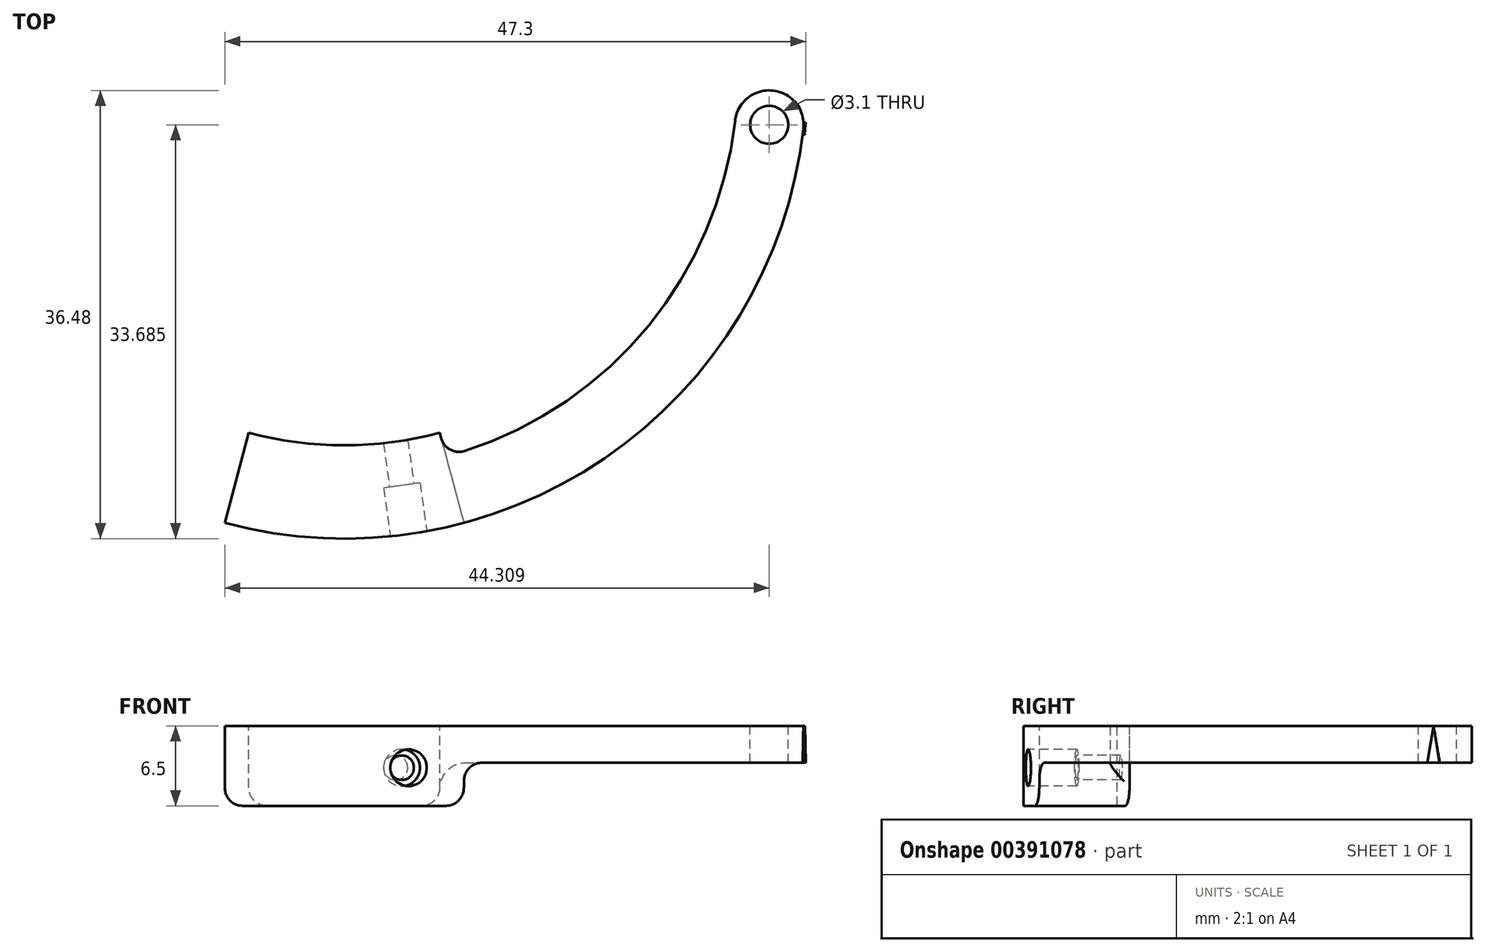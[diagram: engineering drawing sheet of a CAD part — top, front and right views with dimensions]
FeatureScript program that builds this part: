
annotation { "Feature Type Name" : "Feature", "Feature Type Description" : "" }
export const myFeature = defineFeature(function(context is Context, id is Id, definition is map)
    precondition{}
    {
        {
            var Q0;
            Q0=qCreatedBy(makeId("Top.planeOp"),FACE);
            var sketch = newSketch(context, id + "F0", { "sketchPlane" : qUnion([Q0])});
            skCircle(sketch, "E0", {"center": v(0, 0) * mm, "radius": 32 * mm});
            skCircle(sketch, "E1", {"center": v(0, 0) * mm, "radius": 37.6 * mm});
            skLineSegment(sketch, "E2", {"start": v(0, 0) * mm, "end": v(37.36, -4.23) * mm, "construction": true});
            skLineSegment(sketch, "E3", {"start": v(-4.66, -33.17) * mm, "end": v(-4.77, -33.97) * mm, "construction": true});
            skArc(sketch, "E4", {"start": v(-5.56, -33.85) * mm, "mid": v(-5.17, -33.9) * mm, "end": v(-4.77, -33.97) * mm, "construction": true});
            skLineSegment(sketch, "E5", {"start": v(-8.28, -30.9) * mm, "end": v(-9.73, -36.32) * mm});
            skLineSegment(sketch, "E6", {"start": v(0, 0) * mm, "end": v(9.73, -36.32) * mm});
            skPoint(sketch, "E7", {"position": v(34.58, -3.92) * mm});
            skArc(sketch, "E8", {"start": v(37.36, -4.23) * mm, "mid": v(34.9, -1.13) * mm, "end": v(31.8, -3.6) * mm});
            skLineSegment(sketch, "E9", {"start": v(30.07, -10.94) * mm, "end": v(35.33, -12.86) * mm, "construction": true});
            skCircle(sketch, "E10", {"center": v(34.58, -3.92) * mm, "radius": 1.55 * mm});
            skCircle(sketch, "E11", {"center": v(0, 0) * mm, "radius": 30 * mm});
            skLineSegment(sketch, "E12", {"start": v(-8.28, -30.9) * mm, "end": v(-7.76, -28.98) * mm});
            skLineSegment(sketch, "E13", {"start": v(0, 0) * mm, "end": v(4.18, -29.7) * mm, "construction": true});
            skLineSegment(sketch, "E14", {"start": v(0, 0) * mm, "end": v(-4.18, -29.7) * mm, "construction": true});
            skSolve(sketch);
        }
        {
            var Q0;
            {var subQ0=sQuery(id+"F0.wireOp",EDGE,"E8");Q0=makeQuery(id+"F0.imprint","IMPRINT",FACE,{"disambiguationData":[TD([[makeQuery(id+"F0.imprint","IMPRINT",EDGE,{"derivedFrom":subQ0}),1.0]])]});}
            var Q1;
            Q1=makeQuery(id+"F0.imprint","IMPRINT",FACE,{"disambiguationData":[TD([[makeQuery(id+"F0.imprint","IMPRINT",EDGE,{"derivedFrom":sQuery(id+"F0.wireOp",EDGE,"z00oiAul-z2WD-jYly-T4Gg-m5JlJ8elssB2")}),-1.0]])]});
            var Q2;
            Q2=makeQuery(id+"F0.imprint","IMPRINT",FACE,{"disambiguationData":[TD([[makeQuery(id+"F0.imprint","IMPRINT",EDGE,{"derivedFrom":sQuery(id+"F0.wireOp",EDGE,"cpbOuPma-2R4H-8ffu-GBJo-bnfGFGacq3pO")}),-1.0]])]});
            var Q3;
            {var subQ0=sQuery(id+"F0.wireOp",EDGE,"E5");Q3=makeQuery(id+"F0.imprint","IMPRINT",FACE,{"disambiguationData":[TD([[makeQuery(id+"F0.imprint","IMPRINT",EDGE,{"derivedFrom":subQ0}),1.0]])]});}
            extrude(context, id + "F1", {"entities" : qUnion([Q0, Q1, Q2, Q3]), "oppositeDirection" : true, "depth" : 3 * mm});
        }
        {
            var Q0;
            {var subQ0=sQuery(id+"F0.wireOp",EDGE,"E12");Q0=makeQuery(id+"F0.imprint","IMPRINT",FACE,{"disambiguationData":[TD([[makeQuery(id+"F0.imprint","IMPRINT",EDGE,{"derivedFrom":subQ0}),-1.0]])]});}
            var Q1;
            {var subQ0=sQuery(id+"F0.wireOp",EDGE,"E5");Q1=makeQuery(id+"F0.imprint","IMPRINT",FACE,{"disambiguationData":[TD([[makeQuery(id+"F0.imprint","IMPRINT",EDGE,{"derivedFrom":subQ0}),1.0]])]});}
            extrude(context, id + "F2", {"entities" : qUnion([Q0, Q1]), "operationType" : NewBodyOperationType.ADD, "oppositeDirection" : true, "depth" : 6.5 * mm});
        }
        {
            var Q0;
            {var subQ0=sQuery(id+"F0.wireOp",EDGE,"E5");Q0=makeQuery(id+"F0.imprint","IMPRINT",FACE,{"disambiguationData":[TD([[makeQuery(id+"F0.imprint","IMPRINT",EDGE,{"derivedFrom":subQ0}),1.0]])]});}
            cPlane(context, id + "F3", {"entities" : qUnion([Q0]), "cplaneType" : CPlaneType.OFFSET, "offset" : 3.4 * mm, "oppositeDirection" : true, "width" : 150 * mm, "height" : 150 * mm});
        }
        {
            var Q0;
            Q0=qCreatedBy(id+"F3.planeOp",FACE);
            var sketch = newSketch(context, id + "F4", { "sketchPlane" : qUnion([Q0])});
            skPoint(sketch, "E15.0", {"position": v(4.18, -29.7) * mm});
            skLineSegment(sketch, "E15.1", {"start": v(0, 0) * mm, "end": v(4.18, -29.7) * mm, "construction": true});
            skArc(sketch, "E16.1", {"start": v(-7.76, -28.98) * mm, "mid": v(0, -30) * mm, "end": v(7.76, -28.98) * mm});
            skArc(sketch, "E17.0", {"start": v(-9.73, -36.32) * mm, "mid": v(21.17, -31.07) * mm, "end": v(37.36, -4.23) * mm});
            skLineSegment(sketch, "E18", {"start": v(4.18, -29.7) * mm, "end": v(5.23, -37.23) * mm, "construction": true});
            skSolve(sketch);
        }
        {
            var Q0;
            Q0=sQuery(id+"F4.wireOp",VERTEX,"E15.0");
            var Q1;
            Q1=sQuery(id+"F4.wireOp",EDGE,"E15.1");
            cPlane(context, id + "F5", {"entities" : qUnion([Q0, Q1]), "cplaneType" : CPlaneType.LINE_POINT, "offset" : 25 * mm, "width" : 150 * mm, "height" : 150 * mm});
        }
        {
            var Q0;
            Q0=qCreatedBy(id+"F5.planeOp",FACE);
            var sketch = newSketch(context, id + "F6", { "sketchPlane" : qUnion([Q0])});
            skPoint(sketch, "E19.0", {"position": v(0, -3.4) * mm});
            skCircle(sketch, "E20", {"center": v(0, -3.4) * mm, "radius": 1 * mm});
            skSolve(sketch);
        }
        {
            var Q0;
            Q0 = qSketchRegion(id + "F6", true);
            extrude(context, id + "F7", {"entities" : qUnion([Q0]), "operationType" : NewBodyOperationType.REMOVE, "endBound" : BoundingType.SYMMETRIC, "oppositeDirection" : true, "depth" : 25 * mm, "offsetDistance" : 25 * mm});
        }
        {
            var Q0;
            Q0=makeQuery(id+"F2.opExtrude","CAP_EDGE",EDGE,{"disambiguationData":[OSD([sQuery(id+"F0.wireOp",EDGE,"E5"),sQuery(id+"F0.wireOp",EDGE,"E12")])],"isStart":false});
            var Q1;
            Q1=makeQuery(id+"F2.opExtrude","CAP_EDGE",EDGE,{"disambiguationData":[OSD([sQuery(id+"F0.wireOp",EDGE,"E6")])],"isStart":false});
            var Q2;
            Q2=makeQuery(id+"F2.boolean.opBoolean","INTERSECT",EDGE,{"derivedFrom":[makeQuery(id+"F1.opExtrude","CAP_FACE",FACE,{"disambiguationData":[OSD([sQuery(id+"F0.wireOp",EDGE,"E0"),sQuery(id+"F0.wireOp",EDGE,"E1"),sQuery(id+"F0.wireOp",EDGE,"E5"),sQuery(id+"F0.wireOp",EDGE,"E8"),sQuery(id+"F0.wireOp",EDGE,"cpbOuPma-2R4H-8ffu-GBJo-bnfGFGacq3pO")])],"isStart":false}),makeQuery(id+"F2.opExtrude","SWEPT_FACE",FACE,{"disambiguationData":[OSD([sQuery(id+"F0.wireOp",EDGE,"E6")])]})]});
            var Q3;
            Q3=makeQuery(id+"F2.boolean.opBoolean","INTERSECT",EDGE,{"derivedFrom":[makeQuery(id+"F1.opExtrude","SWEPT_FACE",FACE,{"disambiguationData":[OSD([sQuery(id+"F0.wireOp",EDGE,"E0")])]}),makeQuery(id+"F2.opExtrude","SWEPT_FACE",FACE,{"disambiguationData":[OSD([sQuery(id+"F0.wireOp",EDGE,"E6")])]})]});
            fillet(context, id + "F8", {"entities" : qUnion([Q0, Q1, Q2, Q3]), "radius" : 1.5 * mm, "tangentPropagation" : true, "allowEdgeOverflow" : false});
        }
        {
            var Q0;
            Q0=sQuery(id+"F4.wireOp",VERTEX,"E18.end");
            var Q1;
            Q1=sQuery(id+"F4.wireOp",EDGE,"E18");
            cPlane(context, id + "F9", {"entities" : qUnion([Q0, Q1]), "cplaneType" : CPlaneType.LINE_POINT, "offset" : 25 * mm, "width" : 150 * mm, "height" : 150 * mm});
        }
        {
            var Q0;
            Q0=qCreatedBy(id+"F9.planeOp",FACE);
            var sketch = newSketch(context, id + "F10", { "sketchPlane" : qUnion([Q0])});
            skPoint(sketch, "E21.0", {"position": v(0, -3.4) * mm});
            skCircle(sketch, "E22", {"center": v(0, -3.4) * mm, "radius": 1.5 * mm});
            skSolve(sketch);
        }
        {
            var Q0;
            Q0=makeQuery(id+"F10.imprint","IMPRINT",FACE,{"disambiguationData":[TD([[makeQuery(id+"F10.imprint","IMPRINT",EDGE,{"derivedFrom":sQuery(id+"F10.wireOp",EDGE,"E22")}),1.0]])]});
            extrude(context, id + "F11", {"entities" : qUnion([Q0]), "operationType" : NewBodyOperationType.REMOVE, "oppositeDirection" : true, "depth" : 4 * mm, "offsetDistance" : 25 * mm});
        }
        {
            var Q0;
            Q0=sQuery(id+"F0.wireOp",EDGE,"E2");
            var Q1;
            Q1=sQuery(id+"F4.wireOp",VERTEX,"E17.0.end");
            cPlane(context, id + "F12", {"entities" : qUnion([Q0, Q1]), "cplaneType" : CPlaneType.LINE_POINT, "offset" : 25 * mm, "width" : 150 * mm, "height" : 150 * mm});
        }
        {
            var Q0;
            Q0=qCreatedBy(id+"F12.planeOp",FACE);
            var sketch = newSketch(context, id + "F13", { "sketchPlane" : qUnion([Q0])});
            skLineSegment(sketch, "E23.0", {"start": v(-34.42, -3) * mm, "end": v(0, -3) * mm});
            skLineSegment(sketch, "E24.0", {"start": v(0, -3) * mm, "end": v(2.8, -3) * mm});
            skLineSegment(sketch, "E25", {"start": v(0, 0) * mm, "end": v(-0.5, -3) * mm});
            skLineSegment(sketch, "E26", {"start": v(-0.5, -3) * mm, "end": v(0.5, -3) * mm});
            skLineSegment(sketch, "E27", {"start": v(0.5, -3) * mm, "end": v(0, 0) * mm});
            skSolve(sketch);
        }
        {
            var Q0;
            Q0=makeQuery(id+"F13.imprint","IMPRINT",FACE,{"disambiguationData":[TD([[makeQuery(id+"F13.imprint","IMPRINT",EDGE,{"derivedFrom":sQuery(id+"F13.wireOp",EDGE,"E25")}),1.0]])]});
            extrude(context, id + "F14", {"entities" : qUnion([Q0]), "operationType" : NewBodyOperationType.ADD, "endBound" : BoundingType.SYMMETRIC, "depth" : .3 * mm, "offsetDistance" : 25 * mm});
        }
    });
